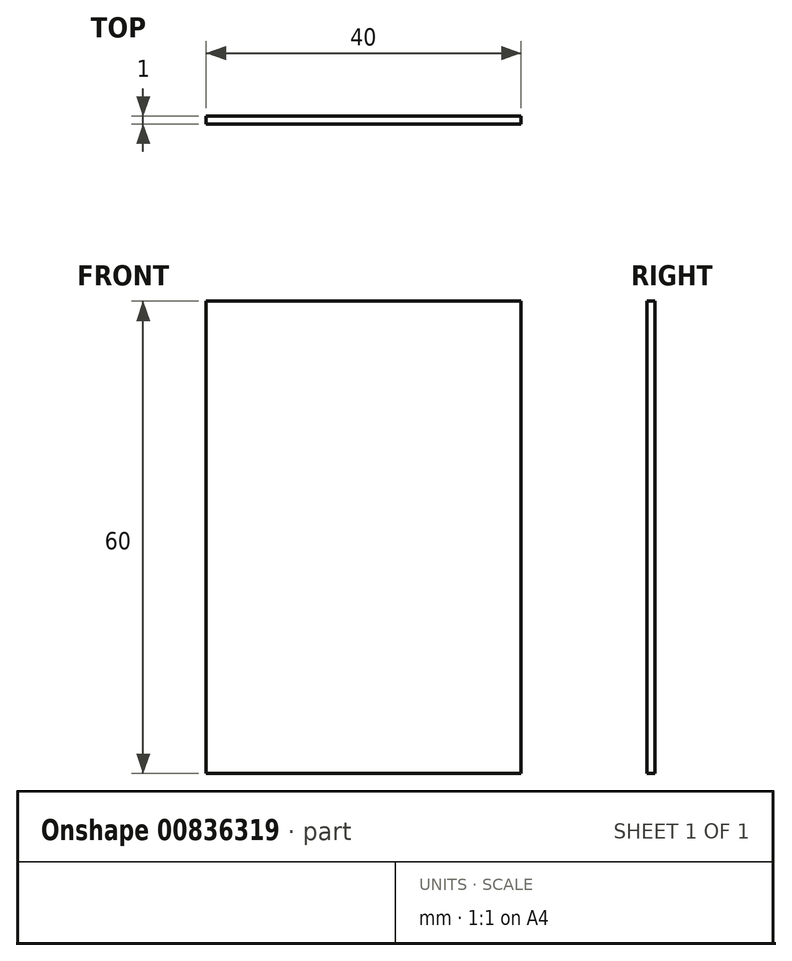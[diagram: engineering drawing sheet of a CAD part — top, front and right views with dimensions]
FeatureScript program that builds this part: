
annotation { "Feature Type Name" : "Feature", "Feature Type Description" : "" }
export const myFeature = defineFeature(function(context is Context, id is Id, definition is map)
    precondition{}
    {
        {
            var Q0;
            Q0=qCreatedBy(makeId("Front.planeOp"),FACE);
            var sketch = newSketch(context, id + "F0", { "sketchPlane" : qUnion([Q0])});
            skLineSegment(sketch, "E0.bottom", {"start": v(20, 30) * mm, "end": v(-20, 30) * mm});
            skLineSegment(sketch, "E0.top", {"start": v(20, -30) * mm, "end": v(-20, -30) * mm});
            skLineSegment(sketch, "E0.left", {"start": v(20, 30) * mm, "end": v(20, -30) * mm});
            skLineSegment(sketch, "E0.right", {"start": v(-20, 30) * mm, "end": v(-20, -30) * mm});
            skPoint(sketch, "E0.middle", {"position": v(0, 0) * mm});
            skSolve(sketch);
        }
        {
            var Q0;
            Q0=qSketchRegion(id+"F0",true);
            extrude(context, id + "F1", {"entities" : qUnion([Q0]), "depth" : 1 * mm, "offsetDistance" : 25 * mm});
        }
    });
